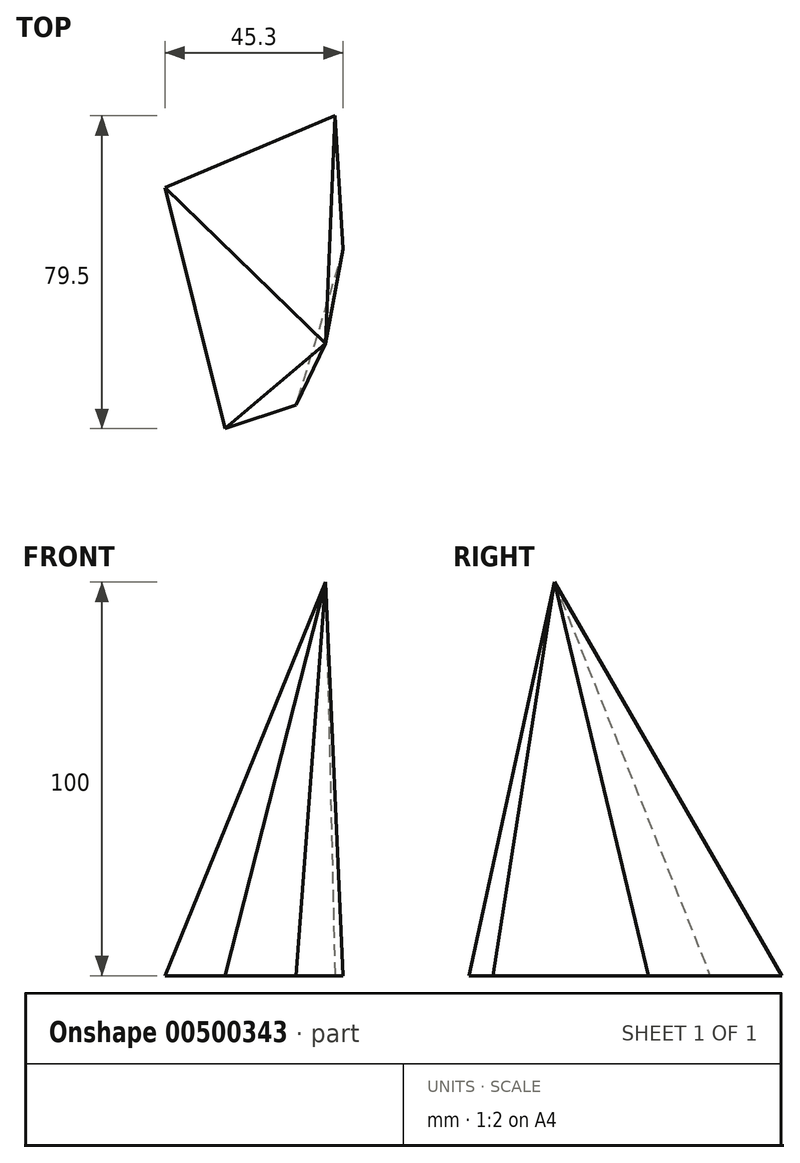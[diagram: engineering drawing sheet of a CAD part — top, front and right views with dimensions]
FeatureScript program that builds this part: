
annotation { "Feature Type Name" : "Feature", "Feature Type Description" : "" }
export const myFeature = defineFeature(function(context is Context, id is Id, definition is map)
    precondition{}
    {
        {
            var Q0;
            Q0=qCreatedBy(makeId("Top.planeOp"),FACE);
            var sketch = newSketch(context, id + "F0", { "sketchPlane" : qUnion([Q0])});
            skLineSegment(sketch, "E0", {"start": v(-25.5, -30.75) * mm, "end": v(-40.8, 30.45) * mm});
            skLineSegment(sketch, "E1", {"start": v(-40.8, 30.45) * mm, "end": v(2.4, 48.75) * mm});
            skLineSegment(sketch, "E2", {"start": v(2.4, 48.75) * mm, "end": v(4.5, 14.85) * mm});
            skLineSegment(sketch, "E3", {"start": v(4.5, 14.85) * mm, "end": v(-7.5, -24.75) * mm});
            skLineSegment(sketch, "E4", {"start": v(-7.5, -24.75) * mm, "end": v(-25.5, -30.75) * mm});
            skSolve(sketch);
        }
        {
            var Q0;
            Q0=qCreatedBy(makeId("Top.planeOp"),FACE);
            cPlane(context, id + "F1", {"entities" : qUnion([Q0]), "cplaneType" : CPlaneType.OFFSET, "offset" : 100 * mm, "width" : 150 * mm, "height" : 150 * mm});
        }
        {
            var Q0;
            Q0=qCreatedBy(id+"F1.planeOp",FACE);
            var sketch = newSketch(context, id + "F2", { "sketchPlane" : qUnion([Q0])});
            skPoint(sketch, "E5", {"position": v(0, -9.09) * mm});
            skSolve(sketch);
        }
        {
            var Q0;
            Q0=sQuery(id+"F2.wireOp",VERTEX,"E5");
            var Q1;
            Q1=makeQuery(id+"F0.imprint","IMPRINT",FACE,{"disambiguationData":[TD([[makeQuery(id+"F0.imprint","IMPRINT",EDGE,{"derivedFrom":sQuery(id+"F0.wireOp",EDGE,"E0")}),-1.0]])]});
            loft(context, id + "F3", {"sheetProfilesArray" : [{ "sheetProfileEntities" : qUnion([Q0]) }, { "sheetProfileEntities" : qUnion([Q1]) }]});
        }
    });
